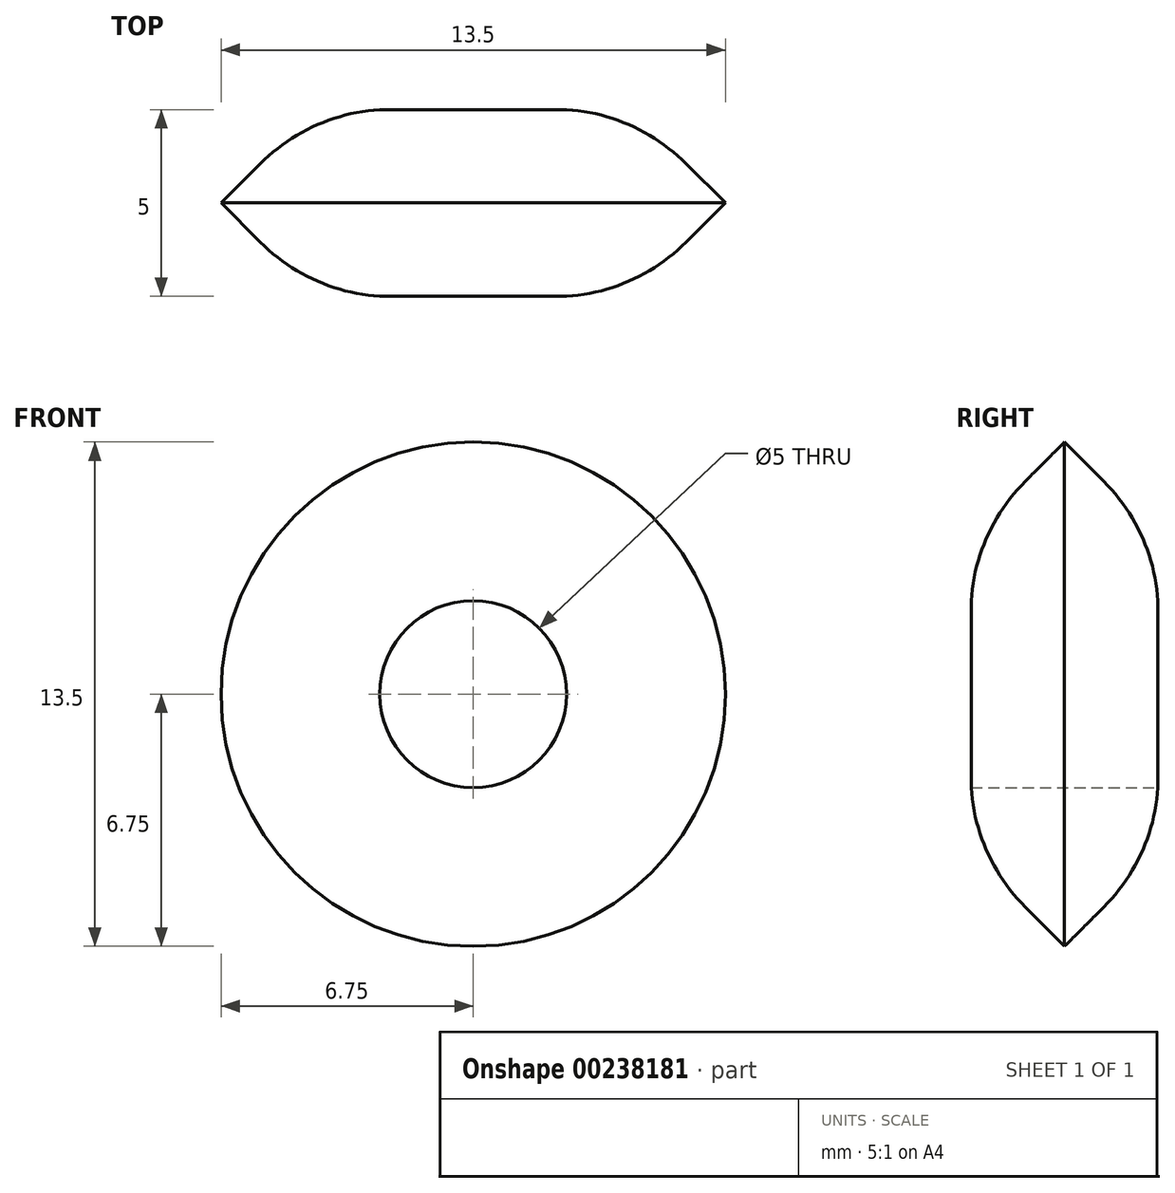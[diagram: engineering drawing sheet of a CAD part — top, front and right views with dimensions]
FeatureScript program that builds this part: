
annotation { "Feature Type Name" : "Feature", "Feature Type Description" : "" }
export const myFeature = defineFeature(function(context is Context, id is Id, definition is map)
    precondition{}
    {
        {
            var Q0;
            Q0=qCreatedBy(makeId("Front.planeOp"),FACE);
            var sketch = newSketch(context, id + "F0", { "sketchPlane" : qUnion([Q0])});
            skCircle(sketch, "E0", {"center": v(0, 0) * mm, "radius": 6.75 * mm});
            skCircle(sketch, "E1", {"center": v(0, 0) * mm, "radius": 2.5 * mm});
            skSolve(sketch);
        }
        {
            var Q0;
            Q0=makeQuery(id+"F0.imprint","IMPRINT",FACE,{"disambiguationData":[TD([[makeQuery(id+"F0.imprint","IMPRINT",EDGE,{"derivedFrom":sQuery(id+"F0.wireOp",EDGE,"E0")}),1.0]])]});
            extrude(context, id + "F1", {"entities" : qUnion([Q0]), "depth" : 5 * mm, "offsetDistance" : 25 * mm});
        }
        {
            var Q0;
            Q0=makeQuery(id+"F1.opExtrude","CAP_EDGE",EDGE,{"disambiguationData":[OSD([sQuery(id+"F0.wireOp",EDGE,"E0")])],"isStart":true});
            var Q1;
            Q1=makeQuery(id+"F1.opExtrude","CAP_EDGE",EDGE,{"disambiguationData":[OSD([sQuery(id+"F0.wireOp",EDGE,"E0")])],"isStart":false});
            chamfer(context, id + "F2", {"entities" : qUnion([Q0, Q1]), "width" : 2.5 * mm, "tangentPropagation" : true});
        }
        {
            var Q0;
            {var subQ0=sQuery(id+"F0.wireOp",EDGE,"E0");Q0=makeQuery(id+"F2.opChamfer","BLEND_EDGE",EDGE,{"blendedFrom":[makeQuery(id+"F1.opExtrude","CAP_EDGE",EDGE,{"disambiguationData":[OSD([subQ0])],"isStart":false}),makeQuery(id+"F1.opExtrude","CAP_FACE",FACE,{"disambiguationData":[OSD([subQ0,sQuery(id+"F0.wireOp",EDGE,"E1")])],"isStart":false})],"blendedInto":[makeQuery(id+"F1.opExtrude","CAP_FACE",FACE,{"disambiguationData":[OSD([subQ0,sQuery(id+"F0.wireOp",EDGE,"E1")])],"isStart":false})]});}
            var Q1;
            {var subQ0=sQuery(id+"F0.wireOp",EDGE,"E0");Q1=makeQuery(id+"F2.opChamfer","BLEND_EDGE",EDGE,{"blendedFrom":[makeQuery(id+"F1.opExtrude","CAP_EDGE",EDGE,{"disambiguationData":[OSD([subQ0])],"isStart":true}),makeQuery(id+"F1.opExtrude","CAP_FACE",FACE,{"disambiguationData":[OSD([subQ0,sQuery(id+"F0.wireOp",EDGE,"E1")])],"isStart":true})],"blendedInto":[makeQuery(id+"F1.opExtrude","CAP_FACE",FACE,{"disambiguationData":[OSD([subQ0,sQuery(id+"F0.wireOp",EDGE,"E1")])],"isStart":true})]});}
            fillet(context, id + "F3", {"entities" : qUnion([Q0, Q1]), "radius" : 5 * mm, "tangentPropagation" : true, "allowEdgeOverflow" : false});
        }
    });
